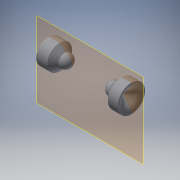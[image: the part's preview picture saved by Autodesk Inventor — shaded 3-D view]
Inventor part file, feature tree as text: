
AUTODESK INVENTOR PART (.ipt)
format: ipt  version: 2019 (Build 230136000, 136)  size: 161,280 bytes
history: native  units: mm
features: reference x5, other x3, plane x1, revolve x1, sketch x1
ambient origin geometry x8: Origin, YZ Plane, XZ Plane, XY Plane, X Axis, Y Axis, Z Axis, Center Point
bodies: Body1 (feature_tree)
feature tree (11):
  plane  "Work Plane1"
  revolve  "Revolution3"  [1 undecoded]
  sketch  "Sketch1"  dims[d5=90.0deg d6=34.557519mm]
  reference  "Reference1"
  reference  "Reference2"
  reference  "Reference3"
  reference  "Reference4"
  reference  "Reference5"
  parser-record x1  (decoder bookkeeping rows leaked as tree rows — omitted from the tree; the rows remain in map.json)
  other  "mount assem.iam"
  other  "mounter:1"
note: 1 file-system path scrubbed to <path> (originals preserved in map.json)
note: 1 required parameter value undecoded (feature->parameter linkage not recoverable at this tier; creation-order binding heuristic only, values carry confidence <= 0.55)
